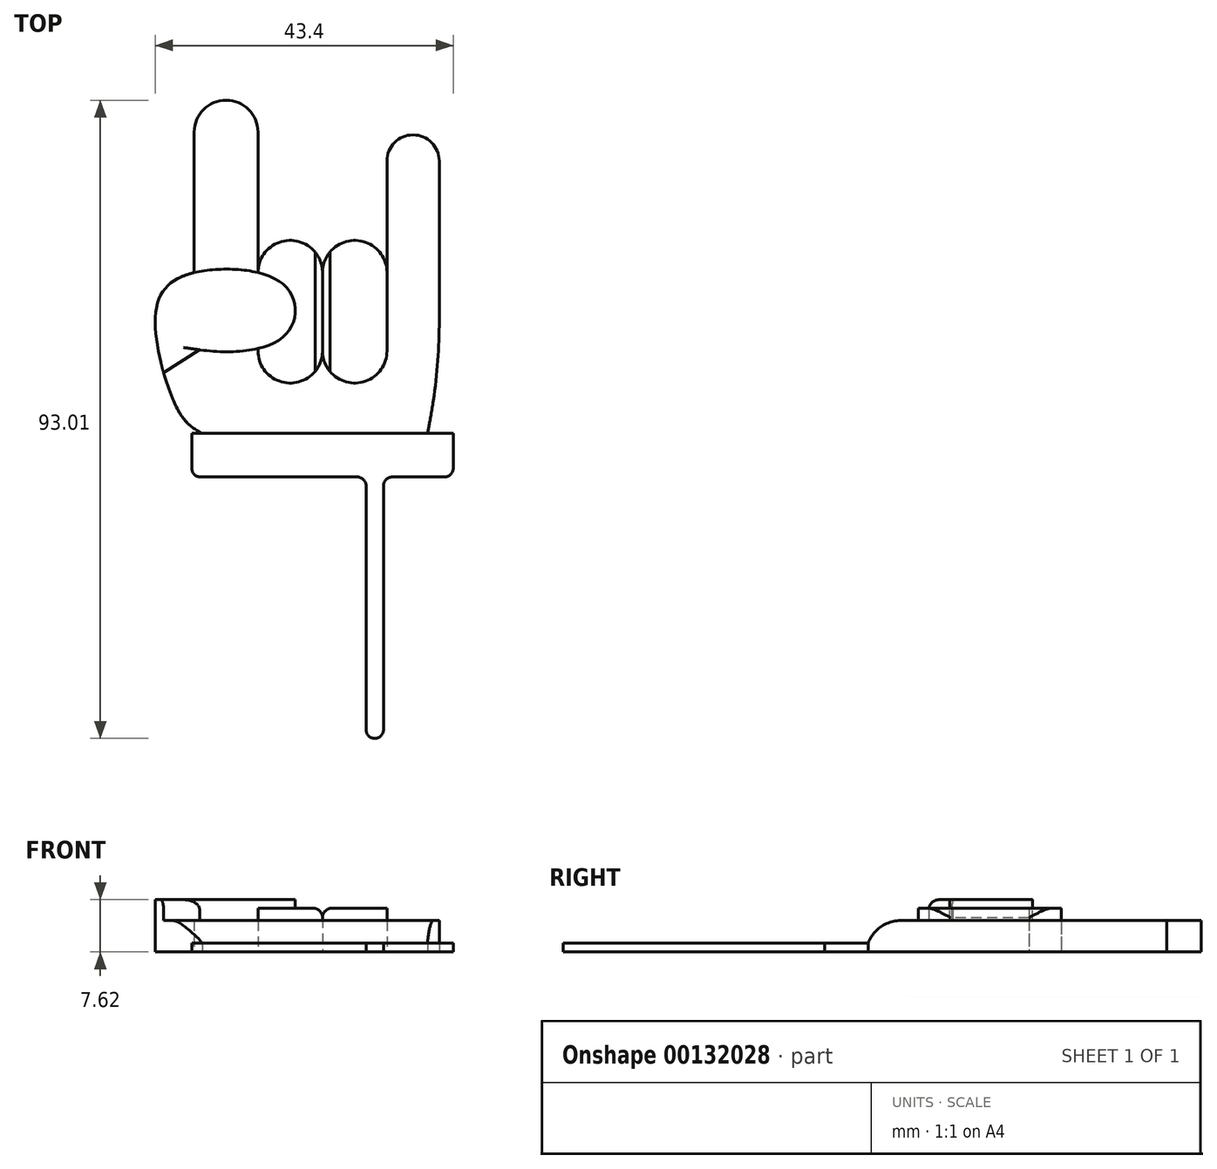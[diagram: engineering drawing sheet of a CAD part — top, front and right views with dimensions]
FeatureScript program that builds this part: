
annotation { "Feature Type Name" : "Feature", "Feature Type Description" : "" }
export const myFeature = defineFeature(function(context is Context, id is Id, definition is map)
    precondition{}
    {
        {
            var Q0;
            Q0=qCreatedBy(makeId("Top.planeOp"),FACE);
            var sketch = newSketch(context, id + "F0", { "sketchPlane" : qUnion([Q0])});
            skLineSegment(sketch, "E0.bottom", {"start": v(-19.05, 0) * mm, "end": v(19.05, 0) * mm});
            skLineSegment(sketch, "E0.top", {"start": v(-19.05, -6.35) * mm, "end": v(19.05, -6.35) * mm});
            skLineSegment(sketch, "E0.left", {"start": v(-19.05, 0) * mm, "end": v(-19.05, -6.35) * mm});
            skLineSegment(sketch, "E0.right", {"start": v(19.05, 0) * mm, "end": v(19.05, -6.35) * mm});
            skPoint(sketch, "E1", {"position": v(0, 0) * mm});
            skLineSegment(sketch, "E2.bottom", {"start": v(-8.9, -6.35) * mm, "end": v(-6.35, -6.35) * mm});
            skLineSegment(sketch, "E2.top", {"start": v(-8.9, -44.45) * mm, "end": v(-6.35, -44.45) * mm});
            skLineSegment(sketch, "E2.left", {"start": v(-8.9, -6.35) * mm, "end": v(-8.9, -44.45) * mm});
            skLineSegment(sketch, "E2.right", {"start": v(-6.35, -6.35) * mm, "end": v(-6.35, -44.45) * mm});
            skLineSegment(sketch, "E3.bottom", {"start": v(-1.27, -6.35) * mm, "end": v(1.27, -6.35) * mm});
            skLineSegment(sketch, "E3.top", {"start": v(-1.27, -44.45) * mm, "end": v(1.27, -44.45) * mm});
            skLineSegment(sketch, "E3.left", {"start": v(-1.27, -6.35) * mm, "end": v(-1.27, -44.45) * mm});
            skLineSegment(sketch, "E3.right", {"start": v(1.27, -6.35) * mm, "end": v(1.27, -44.45) * mm});
            skPoint(sketch, "E4", {"position": v(0, -6.35) * mm});
            skLineSegment(sketch, "E5.MirrorCS", {"start": v(6.35, -6.35) * mm, "end": v(6.35, -44.45) * mm});
            skLineSegment(sketch, "E6.MirrorCS", {"start": v(8.9, -6.35) * mm, "end": v(6.35, -6.35) * mm});
            skLineSegment(sketch, "E7.MirrorCS", {"start": v(8.9, -6.35) * mm, "end": v(8.9, -44.45) * mm});
            skLineSegment(sketch, "E8.MirrorCS", {"start": v(8.9, -44.45) * mm, "end": v(6.35, -44.45) * mm});
            skFitSpline(sketch, "E9", {"points": [v(-17.47, 0) * mm, v(-21.92, 5.27) * mm, v(-23.97, 19.17) * mm, v(-17.27, 23.7) * mm, v(-5.22, 21.27) * mm, v(-5.25, 14.52) * mm, v(-17.88, 12.19) * mm], "startDerivative": vector(-48.82, 23.14) * mm, "endDerivative": vector(-77.01, 10.72) * mm});
            skLineSegment(sketch, "E10", {"start": v(-18.68, 23.43) * mm, "end": v(-18.68, 43.92) * mm});
            skLineSegment(sketch, "E11", {"start": v(-9.4, 23.43) * mm, "end": v(-9.4, 43.92) * mm});
            skArc(sketch, "E12", {"start": v(-9.4, 43.92) * mm, "mid": v(-14.04, 48.56) * mm, "end": v(-18.68, 43.92) * mm});
            skArc(sketch, "E13", {"start": v(0, 23.43) * mm, "mid": v(-4.7, 28.13) * mm, "end": v(-9.4, 23.43) * mm});
            skArc(sketch, "E14", {"start": v(9.4, 23.43) * mm, "mid": v(4.7, 28.13) * mm, "end": v(0, 23.43) * mm});
            skLineSegment(sketch, "E15", {"start": v(0, 23.43) * mm, "end": v(0, 12.03) * mm});
            skArc(sketch, "E16", {"start": v(-9.4, 12.03) * mm, "mid": v(-4.7, 7.34) * mm, "end": v(0, 12.03) * mm});
            skLineSegment(sketch, "E17", {"start": v(-9.4, 12.03) * mm, "end": v(-9.4, 12.37) * mm});
            skLineSegment(sketch, "E18", {"start": v(9.4, 23.43) * mm, "end": v(9.4, 12.03) * mm});
            skArc(sketch, "E19", {"start": v(0, 12.03) * mm, "mid": v(4.7, 7.34) * mm, "end": v(9.4, 12.03) * mm});
            skLineSegment(sketch, "E20", {"start": v(9.4, 23.43) * mm, "end": v(9.4, 39.7) * mm});
            skArc(sketch, "E21", {"start": v(17.02, 39.7) * mm, "mid": v(13.2, 43.5) * mm, "end": v(9.4, 39.7) * mm});
            skLineSegment(sketch, "E22", {"start": v(17.02, 39.7) * mm, "end": v(17.02, 16.47) * mm});
            skArc(sketch, "E23", {"start": v(15.3, 0) * mm, "mid": v(16.59, 8.19) * mm, "end": v(17.02, 16.47) * mm});
            skLineSegment(sketch, "E24", {"start": v(-17.88, 12.19) * mm, "end": v(-23.15, 8.82) * mm});
            skSolve(sketch);
        }
        {
            var Q0;
            Q0=makeQuery(id+"F0.imprint","IMPRINT",FACE,{"disambiguationData":[TD([[makeQuery(id+"F0.imprint","IMPRINT",EDGE,{"derivedFrom":sQuery(id+"F0.wireOp",EDGE,"E2.bottom")}),-1.0]])]});
            var Q1;
            Q1=makeQuery(id+"F0.imprint","IMPRINT",FACE,{"disambiguationData":[TD([[makeQuery(id+"F0.imprint","IMPRINT",EDGE,{"derivedFrom":sQuery(id+"F0.wireOp",EDGE,"E3.bottom")}),-1.0]])]});
            var Q2;
            Q2=makeQuery(id+"F0.imprint","IMPRINT",FACE,{"disambiguationData":[TD([[makeQuery(id+"F0.imprint","IMPRINT",EDGE,{"derivedFrom":sQuery(id+"F0.wireOp",EDGE,"E5.MirrorCS")}),1.0]])]});
            var Q3;
            {var subQ0=sQuery(id+"F0.wireOp",EDGE,"E0.left");Q3=makeQuery(id+"F0.imprint","IMPRINT",FACE,{"disambiguationData":[TD([[makeQuery(id+"F0.imprint","IMPRINT",EDGE,{"derivedFrom":subQ0}),1.0]])]});}
            extrude(context, id + "F1", {"entities" : qUnion([Q0, Q1, Q2, Q3]), "depth" : 1.27 * mm});
        }
        {
            var Q0;
            Q0=makeQuery(id+"F1.opExtrude","SWEPT_EDGE",EDGE,{"disambiguationData":[OSD([sQuery(id+"F0.wireOp",EDGE,"E0.top"),sQuery(id+"F0.wireOp",EDGE,"E2.bottom"),sQuery(id+"F0.wireOp",EDGE,"E2.right")])]});
            var Q1;
            Q1=makeQuery(id+"F1.opExtrude","SWEPT_EDGE",EDGE,{"disambiguationData":[OSD([sQuery(id+"F0.wireOp",EDGE,"E2.top"),sQuery(id+"F0.wireOp",EDGE,"E2.right")])]});
            var Q2;
            Q2=makeQuery(id+"F1.opExtrude","SWEPT_EDGE",EDGE,{"disambiguationData":[OSD([sQuery(id+"F0.wireOp",EDGE,"E2.top"),sQuery(id+"F0.wireOp",EDGE,"E2.left")])]});
            var Q3;
            Q3=makeQuery(id+"F1.opExtrude","SWEPT_EDGE",EDGE,{"disambiguationData":[OSD([sQuery(id+"F0.wireOp",EDGE,"E0.top"),sQuery(id+"F0.wireOp",EDGE,"E3.bottom"),sQuery(id+"F0.wireOp",EDGE,"E3.left")])]});
            var Q4;
            Q4=makeQuery(id+"F1.opExtrude","SWEPT_EDGE",EDGE,{"disambiguationData":[OSD([sQuery(id+"F0.wireOp",EDGE,"E0.top"),sQuery(id+"F0.wireOp",EDGE,"E5.MirrorCS"),sQuery(id+"F0.wireOp",EDGE,"E6.MirrorCS")])]});
            var Q5;
            Q5=makeQuery(id+"F1.opExtrude","SWEPT_EDGE",EDGE,{"disambiguationData":[OSD([sQuery(id+"F0.wireOp",EDGE,"E3.top"),sQuery(id+"F0.wireOp",EDGE,"E3.left")])]});
            var Q6;
            Q6=makeQuery(id+"F1.opExtrude","SWEPT_EDGE",EDGE,{"disambiguationData":[OSD([sQuery(id+"F0.wireOp",EDGE,"E3.top"),sQuery(id+"F0.wireOp",EDGE,"E3.right")])]});
            var Q7;
            Q7=makeQuery(id+"F1.opExtrude","SWEPT_EDGE",EDGE,{"disambiguationData":[OSD([sQuery(id+"F0.wireOp",EDGE,"E5.MirrorCS"),sQuery(id+"F0.wireOp",EDGE,"E8.MirrorCS")])]});
            var Q8;
            Q8=makeQuery(id+"F1.opExtrude","SWEPT_EDGE",EDGE,{"disambiguationData":[OSD([sQuery(id+"F0.wireOp",EDGE,"E7.MirrorCS"),sQuery(id+"F0.wireOp",EDGE,"E8.MirrorCS")])]});
            var Q9;
            Q9=makeQuery(id+"F1.opExtrude","SWEPT_EDGE",EDGE,{"disambiguationData":[OSD([sQuery(id+"F0.wireOp",EDGE,"E0.top"),sQuery(id+"F0.wireOp",EDGE,"E3.bottom"),sQuery(id+"F0.wireOp",EDGE,"E3.right")])]});
            var Q10;
            Q10=makeQuery(id+"F1.opExtrude","SWEPT_EDGE",EDGE,{"disambiguationData":[OSD([sQuery(id+"F0.wireOp",EDGE,"E0.top"),sQuery(id+"F0.wireOp",EDGE,"E6.MirrorCS"),sQuery(id+"F0.wireOp",EDGE,"E7.MirrorCS")])]});
            var Q11;
            Q11=makeQuery(id+"F1.opExtrude","SWEPT_EDGE",EDGE,{"disambiguationData":[OSD([sQuery(id+"F0.wireOp",EDGE,"E0.top"),sQuery(id+"F0.wireOp",EDGE,"E2.bottom"),sQuery(id+"F0.wireOp",EDGE,"E2.left")])]});
            fillet(context, id + "F2", {"entities" : qUnion([Q0, Q1, Q2, Q3, Q4, Q5, Q6, Q7, Q8, Q9, Q10, Q11]), "radius" : 1.27 * mm, "tangentPropagation" : true, "allowEdgeOverflow" : false});
        }
        {
            var Q0;
            {var subQ0=sQuery(id+"F0.wireOp",EDGE,"E10");Q0=makeQuery(id+"F0.imprint","IMPRINT",FACE,{"disambiguationData":[TD([[makeQuery(id+"F0.imprint","IMPRINT",EDGE,{"derivedFrom":subQ0}),-1.0]])]});}
            var Q1;
            Q1=makeQuery(id+"F0.imprint","IMPRINT",FACE,{"disambiguationData":[TD([[makeQuery(id+"F0.imprint","IMPRINT",EDGE,{"derivedFrom":sQuery(id+"F0.wireOp",EDGE,"E16")}),-1.0]])]});
            extrude(context, id + "F3", {"entities" : qUnion([Q0, Q1]), "operationType" : NewBodyOperationType.ADD, "depth" : 4.57 * mm});
        }
        {
            var Q0;
            {var subQ0=sQuery(id+"F0.wireOp",EDGE,"E13");Q0=makeQuery(id+"F0.imprint","IMPRINT",FACE,{"disambiguationData":[TD([[makeQuery(id+"F0.imprint","IMPRINT",EDGE,{"derivedFrom":subQ0}),1.0]])]});}
            var Q1;
            Q1=makeQuery(id+"F0.imprint","IMPRINT",FACE,{"disambiguationData":[TD([[makeQuery(id+"F0.imprint","IMPRINT",EDGE,{"derivedFrom":sQuery(id+"F0.wireOp",EDGE,"E14")}),1.0]])]});
            extrude(context, id + "F4", {"entities" : qUnion([Q0, Q1]), "operationType" : NewBodyOperationType.ADD, "depth" : 6.35 * mm});
        }
        {
            var Q0;
            {var subQ0=sQuery(id+"F0.wireOp",EDGE,"E24");Q0=makeQuery(id+"F0.imprint","IMPRINT",FACE,{"disambiguationData":[TD([[makeQuery(id+"F0.imprint","IMPRINT",EDGE,{"derivedFrom":subQ0}),-1.0]])]});}
            extrude(context, id + "F5", {"entities" : qUnion([Q0]), "operationType" : NewBodyOperationType.ADD, "depth" : 7.62 * mm});
        }
        {
            var Q0;
            Q0=makeQuery(id+"F3.opExtrude","CAP_EDGE",EDGE,{"disambiguationData":[OSD([sQuery(id+"F0.wireOp",EDGE,"E24")])],"isStart":false});
            var Q1;
            Q1=makeQuery(id+"F5.opExtrude","CAP_EDGE",EDGE,{"disambiguationData":[OSD([sQuery(id+"F0.wireOp",EDGE,"E24")])],"isStart":false});
            fillet(context, id + "F6", {"entities" : qUnion([Q0, Q1]), "radius" : 1.52 * mm, "tangentPropagation" : true, "allowEdgeOverflow" : false});
        }
        {
            var Q0;
            Q0=makeQuery(id+"F3.opExtrude","CAP_EDGE",EDGE,{"disambiguationData":[OSD([sQuery(id+"F0.wireOp",EDGE,"E0.bottom")])],"isStart":false});
            fillet(context, id + "F7", {"entities" : qUnion([Q0]), "radius" : 5.08 * mm, "tangentPropagation" : true, "allowEdgeOverflow" : false});
        }
        {
            var Q0;
            Q0=qCreatedBy(makeId("Front.planeOp"),FACE);
            var sketch = newSketch(context, id + "F8", { "sketchPlane" : qUnion([Q0])});
            skLineSegment(sketch, "E25", {"start": v(-1.4, 6.38) * mm, "end": v(1.4, 6.38) * mm});
            skPoint(sketch, "E26", {"position": v(0, 6.38) * mm});
            skArc(sketch, "E27", {"start": v(1.4, 6.38) * mm, "mid": v(0.4, 5.98) * mm, "end": v(0, 5) * mm});
            skArc(sketch, "E28", {"start": v(0, 5) * mm, "mid": v(-0.4, 5.98) * mm, "end": v(-1.4, 6.38) * mm});
            skSolve(sketch);
        }
        {
            var Q0;
            Q0 = qSketchRegion(id + "F8", true);
            extrude(context, id + "F9", {"entities" : qUnion([Q0]), "operationType" : NewBodyOperationType.REMOVE, "oppositeDirection" : true, "depth" : 38.1 * mm});
        }
    });
